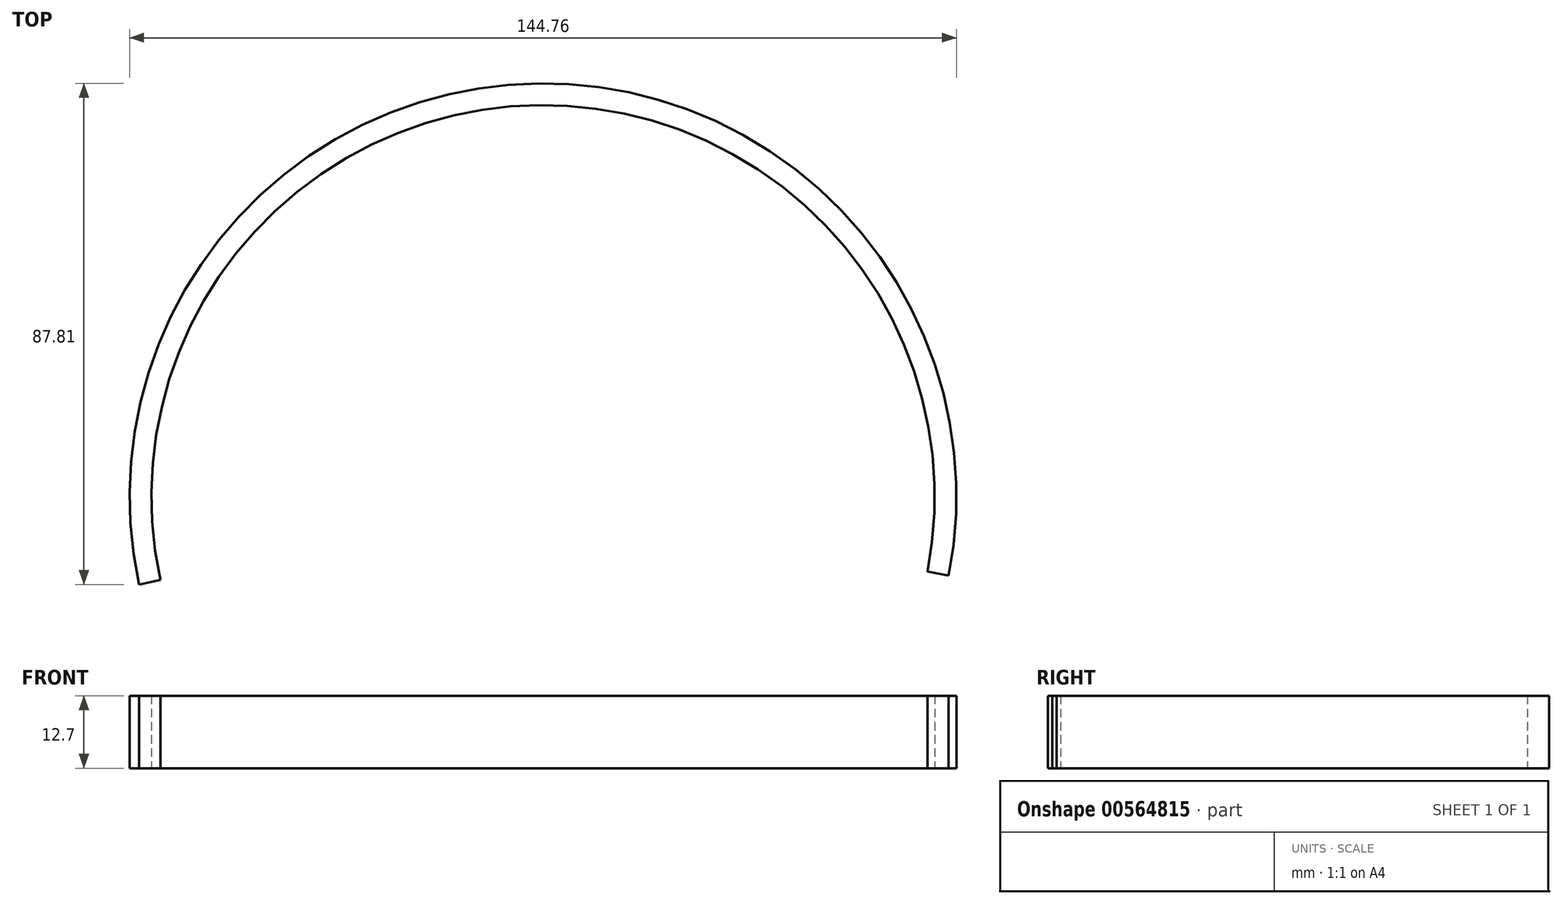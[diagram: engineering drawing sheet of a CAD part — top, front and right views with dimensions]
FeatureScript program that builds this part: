
annotation { "Feature Type Name" : "Feature", "Feature Type Description" : "" }
export const myFeature = defineFeature(function(context is Context, id is Id, definition is map)
    precondition{}
    {
        {
            var Q0;
            Q0=qCreatedBy(makeId("Top.planeOp"),FACE);
            var sketch = newSketch(context, id + "F0", { "sketchPlane" : qUnion([Q0])});
            skArc(sketch, "E0.0", {"start": v(67.3, -13.17) * mm, "mid": v(-0.74, 68.56) * mm, "end": v(-67, -14.62) * mm});
            skArc(sketch, "E1.0", {"start": v(71.03, -13.9) * mm, "mid": v(-0.78, 72.37) * mm, "end": v(-70.71, -15.43) * mm});
            skLineSegment(sketch, "E2", {"start": v(-70.71, -15.43) * mm, "end": v(-67, -14.62) * mm});
            skLineSegment(sketch, "E3", {"start": v(71.03, -13.9) * mm, "end": v(67.3, -13.17) * mm});
            skSolve(sketch);
        }
        {
            var Q0;
            Q0=makeQuery(id+"F0.imprint","IMPRINT",FACE,{"disambiguationData":[TD([[makeQuery(id+"F0.imprint","IMPRINT",EDGE,{"derivedFrom":sQuery(id+"F0.wireOp",EDGE,"E0.0")}),-1.0]])]});
            extrude(context, id + "F1", {"entities" : qUnion([Q0]), "endBound" : BoundingType.SYMMETRIC, "depth" : 12.7 * mm, "offsetDistance" : 25.4 * mm});
        }
    });
